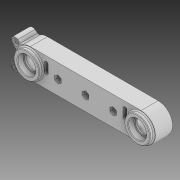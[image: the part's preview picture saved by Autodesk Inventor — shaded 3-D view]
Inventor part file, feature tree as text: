
AUTODESK INVENTOR PART (.ipt)
format: ipt  version: 2020 (Build 240168000, 168)  size: 448,512 bytes
history: native  units: mm
features: extrude x12, sketch x11, projected_geometry x4, chamfer x2, pattern_linear x1, fillet x1
ambient origin geometry x8: Origin, YZ Plane, XZ Plane, XY Plane, X Axis, Y Axis, Z Axis, Center Point
bodies: Solid1 (feature_tree)
feature tree (31):
  extrude  "Extrusion1"  Depth=13.0mm
  extrude  "Extrusion2"  Depth=12.5mm TaperAngle=0.0deg
  extrude  "Extrusion5"  TaperAngle=0.0deg  [1 undecoded]
  extrude  "Extrusion6"  Depth=3.0mm
  extrude  "Extrusion7"  Depth=3.5mm TaperAngle=0.0deg
  chamfer  "Chamfer1"  Distance=5.0mm
  extrude  "Extrusion8"  Depth=1.5mm
  extrude  "Extrusion9"  Depth=3.5mm
  extrude  "Extrusion10"  Depth=0.2mm TaperAngle=0.0deg
  pattern_linear  "Rectangular Pattern1"  Spacing1=1.0mm  [1 undecoded]
  extrude  "Extrusion11"  Depth=1.0mm
  extrude  "Extrusion13"  Depth=25.0mm
  chamfer  "Chamfer2"  Distance=20.0mm
  extrude  "Extrusion15"  Depth=14.5mm
  extrude  "Extrusion14"  Depth=10.0mm TaperAngle=0.0deg
  fillet  "Fillet1"  Radius=4.0mm
  sketch  "Sketch1"  dims[d0=100.3mm d1=13.0mm]
  sketch  "Sketch2"  dims[d2=3.0mm d3=0.0mm d5=12.5mm d6=0.0mm]
  projected_geometry  "Projected Loop1"
  sketch  "Sketch5"  dims[d14=6.0mm d15=0.0mm d16=0.0mm]
  sketch  "Sketch6"  dims[d17=3.0mm d18=16.3mm]
  sketch  "Sketch7"  dims[d19=3.5mm d20=3.5mm d21=0.0mm d22=5.0mm d23=0.0mm]
  sketch  "Sketch8"  dims[d24=1.0mm d25=2.0mm d26=45.0deg d27=1.5mm]
  sketch  "Sketch9"  dims[d28=0.4mm d29=0.0mm d30=3.5mm]
  sketch  "Sketch10"  dims[d31=8.0mm d34=0.2mm d35=0.0mm]
  sketch  "Sketch14"  dims[d36=3.0mm d37=0.0mm]
  projected_geometry  "Projected Loop2"
  projected_geometry  "Projected Loop3"
  projected_geometry  "Projected Loop4"
  sketch  "Sketch15"  dims[d38=1.0mm]
  sketch  "Sketch16"  dims[d39=1.0mm d40=1.0mm d41=1.0mm d42=25.0mm d43=20.0mm d45=100.3mm d47=14.5mm d48=10.0mm d49=0.0mm d50=4.0mm d51=4.0mm d52=4.0mm d53=4.0mm d57=11.5mm d58=0.0mm d59=5.8mm d60=2.0mm d61=0.0mm d62=0.5mm d63=2.0mm d64=45.0deg d65=1.7mm d66=7.0mm d67=25.0mm d68=7.5mm d69=3.2mm d70=10.0mm d71=10.0mm d72=0.0mm d73=2.0mm]
note: 2 required parameter values undecoded (feature->parameter linkage not recoverable at this tier; creation-order binding heuristic only, values carry confidence <= 0.55)
